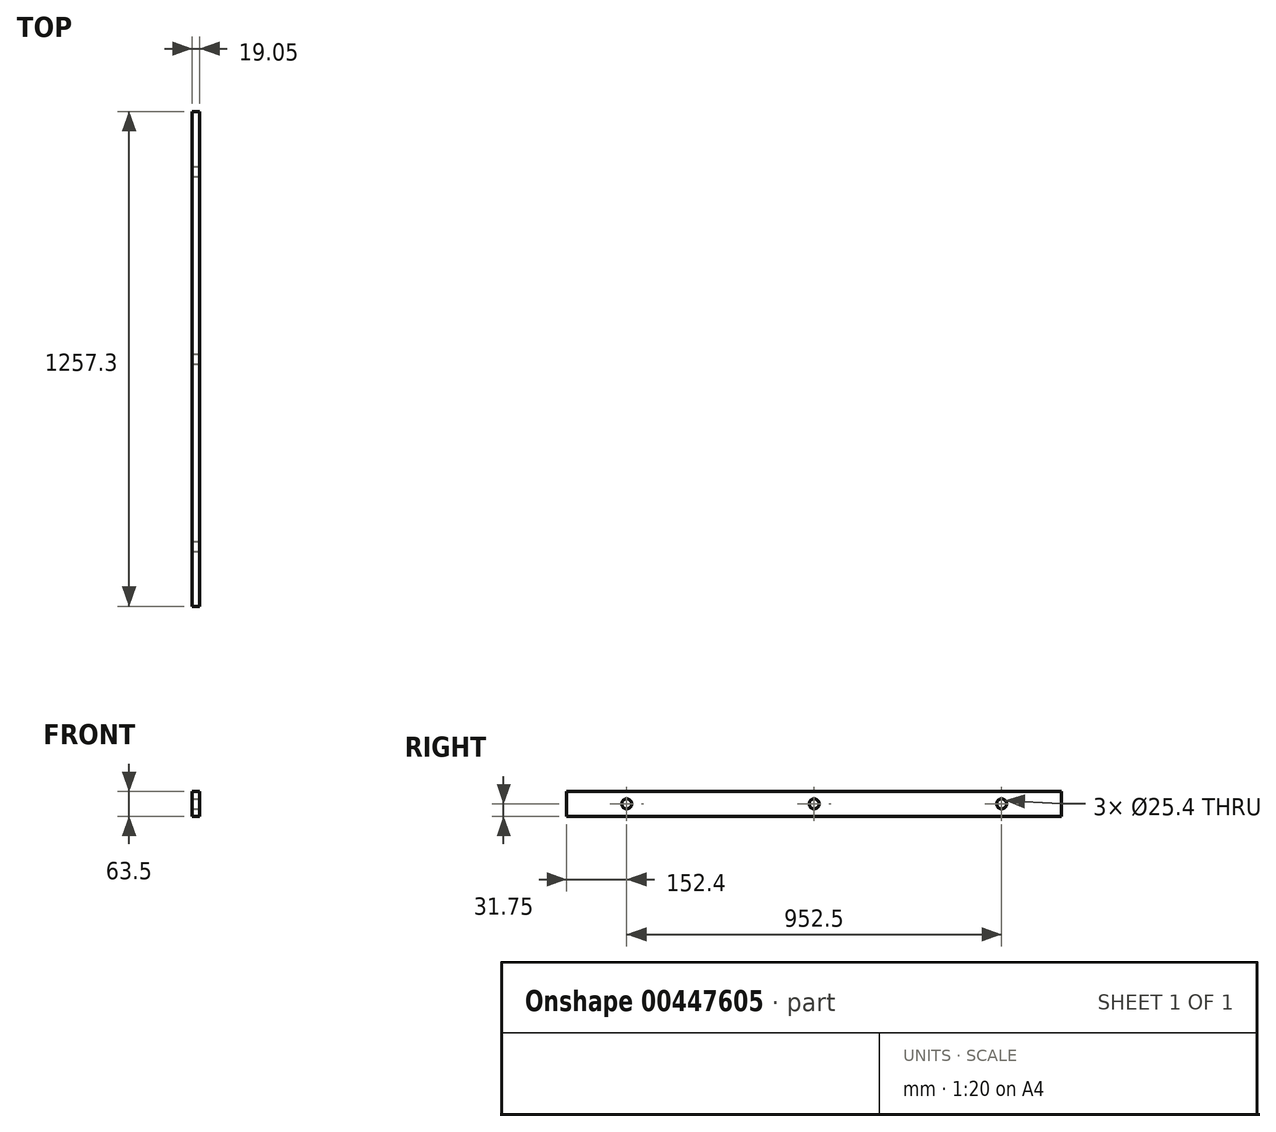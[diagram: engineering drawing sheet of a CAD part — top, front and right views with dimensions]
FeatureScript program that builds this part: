
annotation { "Feature Type Name" : "Feature", "Feature Type Description" : "" }
export const myFeature = defineFeature(function(context is Context, id is Id, definition is map)
    precondition{}
    {
        {
            var Q0;
            Q0=qCreatedBy(makeId("Front.planeOp"),FACE);
            var sketch = newSketch(context, id + "F0", { "sketchPlane" : qUnion([Q0])});
            skLineSegment(sketch, "E0.bottom", {"start": v(0, 0) * mm, "end": v(19.05, 0) * mm});
            skLineSegment(sketch, "E0.top", {"start": v(0, -63.5) * mm, "end": v(19.05, -63.5) * mm});
            skLineSegment(sketch, "E0.left", {"start": v(0, 0) * mm, "end": v(0, -63.5) * mm});
            skLineSegment(sketch, "E0.right", {"start": v(19.05, 0) * mm, "end": v(19.05, -63.5) * mm});
            skSolve(sketch);
        }
        {
            var Q0;
            Q0 = qSketchRegion(id + "F0", true);
            extrude(context, id + "F1", {"entities" : qUnion([Q0]), "depth" : 1257.3 * mm, "offsetDistance" : 25.4 * mm});
        }
        {
            var Q0;
            Q0=makeQuery(id+"F1.opExtrude","SWEPT_FACE",FACE,{"disambiguationData":[OSD([sQuery(id+"F0.wireOp",EDGE,"E0.right")])]});
            var sketch = newSketch(context, id + "F2", { "sketchPlane" : qUnion([Q0])});
            skCircle(sketch, "E1", {"center": v(-1104.9, -31.75) * mm, "radius": 12.7 * mm});
            skCircle(sketch, "E2", {"center": v(-628.65, -31.75) * mm, "radius": 12.7 * mm});
            skCircle(sketch, "E3", {"center": v(-152.4, -31.75) * mm, "radius": 12.7 * mm});
            skSolve(sketch);
        }
        {
            var Q0;
            Q0 = qSketchRegion(id + "F2", true);
            extrude(context, id + "F3", {"entities" : qUnion([Q0]), "operationType" : NewBodyOperationType.REMOVE, "endBound" : BoundingType.THROUGH_ALL, "oppositeDirection" : true, "depth" : 9.52 * mm, "offsetDistance" : 25.4 * mm});
        }
    });
